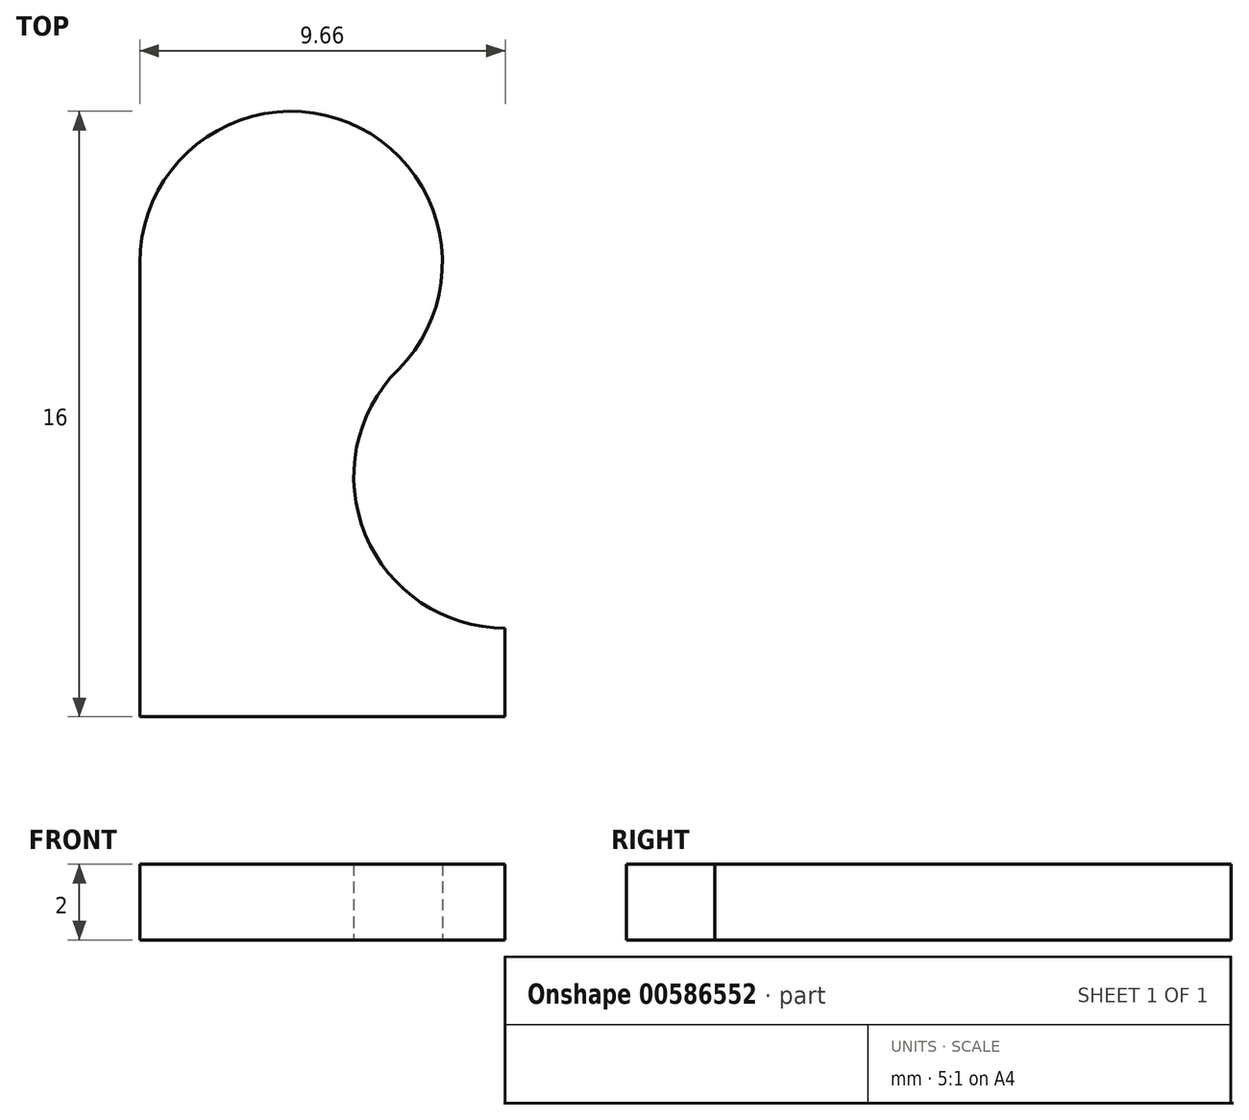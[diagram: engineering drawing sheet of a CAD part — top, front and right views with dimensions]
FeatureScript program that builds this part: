
annotation { "Feature Type Name" : "Feature", "Feature Type Description" : "" }
export const myFeature = defineFeature(function(context is Context, id is Id, definition is map)
    precondition{}
    {
        {
            var Q0;
            Q0=qCreatedBy(makeId("Top.planeOp"),FACE);
            var sketch = newSketch(context, id + "F0", { "sketchPlane" : qUnion([Q0])});
            skLineSegment(sketch, "E0", {"start": v(0, 0) * mm, "end": v(0, 12) * mm});
            skArc(sketch, "E1", {"start": v(0, 12) * mm, "mid": v(5.53, 15.7) * mm, "end": v(6.83, 9.17) * mm});
            skArc(sketch, "E2", {"start": v(6.83, 9.17) * mm, "mid": v(5.96, 4.81) * mm, "end": v(9.66, 2.34) * mm});
            skLineSegment(sketch, "E3", {"start": v(4, 12) * mm, "end": v(9.66, 6.34) * mm, "construction": true});
            skLineSegment(sketch, "E4", {"start": v(9.66, 0) * mm, "end": v(9.66, 6.34) * mm, "construction": true});
            skLineSegment(sketch, "E5", {"start": v(0, 0) * mm, "end": v(9.66, 0) * mm});
            skLineSegment(sketch, "E6", {"start": v(9.66, 2.34) * mm, "end": v(9.66, 0) * mm});
            skLineSegment(sketch, "E7", {"start": v(0, 12) * mm, "end": v(4, 12) * mm, "construction": true});
            skLineSegment(sketch, "E8", {"start": v(4, 12) * mm, "end": v(4, 8) * mm, "construction": true});
            skLineSegment(sketch, "E9", {"start": v(4, 8) * mm, "end": v(4, 4) * mm, "construction": true});
            skLineSegment(sketch, "E10", {"start": v(4, 0) * mm, "end": v(4, 4) * mm, "construction": true});
            skSolve(sketch);
        }
        {
            var Q0;
            Q0=qSketchRegion(id+"F0",true);
            extrude(context, id + "F1", {"entities" : qUnion([Q0]), "depth" : 2 * mm, "offsetDistance" : 25 * mm});
        }
    });
